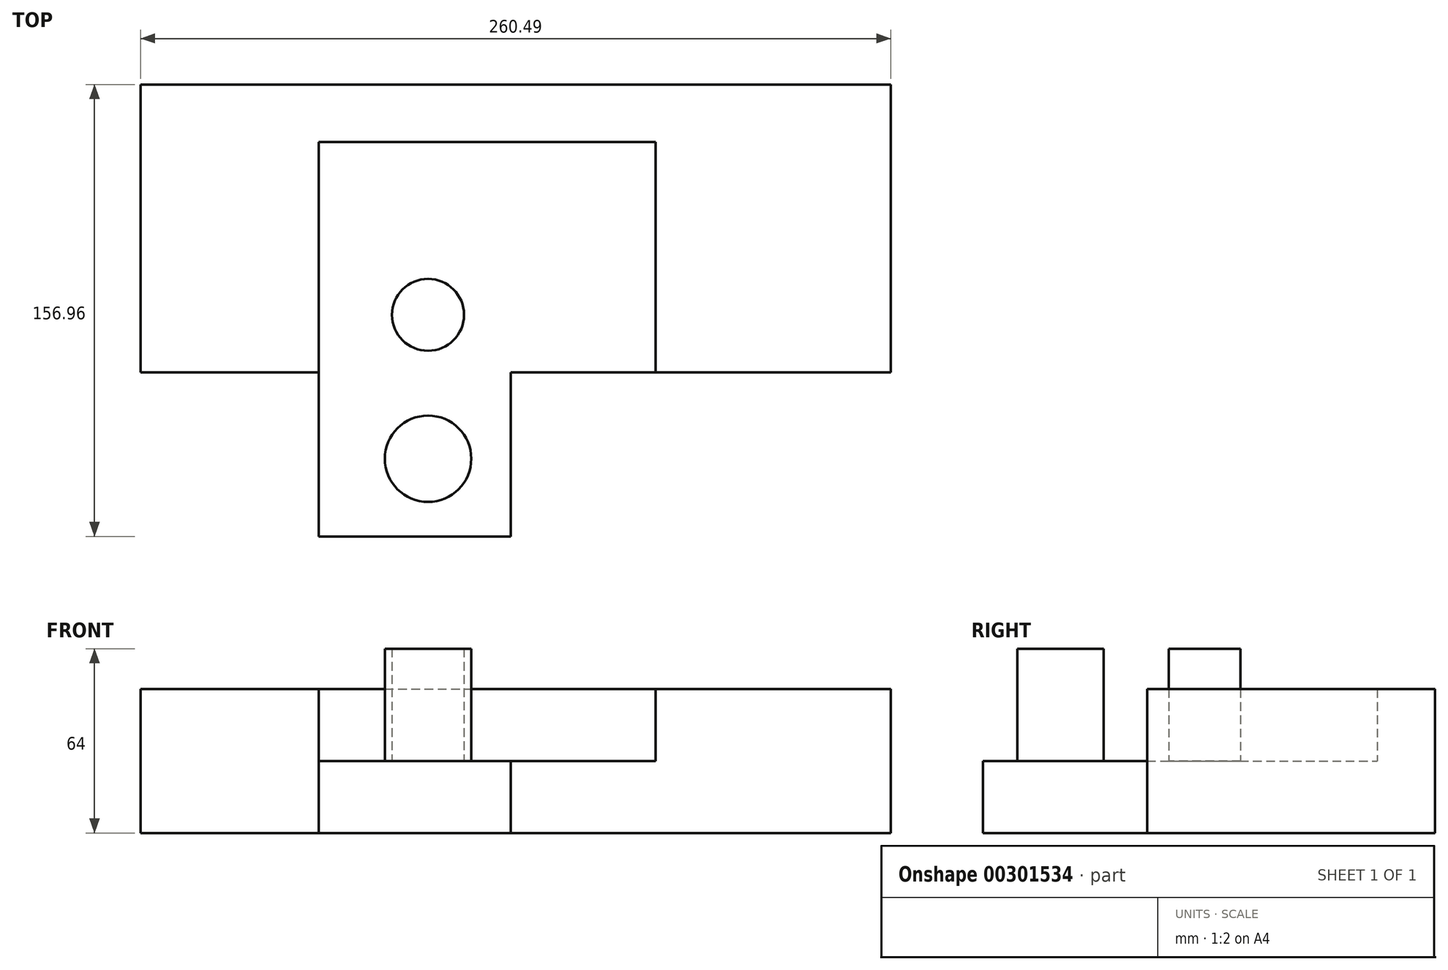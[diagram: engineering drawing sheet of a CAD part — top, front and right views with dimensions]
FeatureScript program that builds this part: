
annotation { "Feature Type Name" : "Feature", "Feature Type Description" : "" }
export const myFeature = defineFeature(function(context is Context, id is Id, definition is map)
    precondition{}
    {
        {
            var Q0;
            Q0=qCreatedBy(makeId("Top.planeOp"),FACE);
            var sketch = newSketch(context, id + "F0", { "sketchPlane" : qUnion([Q0])});
            skLineSegment(sketch, "E0", {"start": v(-120.1, 0) * mm, "end": v(-58.28, 0) * mm});
            skLineSegment(sketch, "E1", {"start": v(-58.28, 0) * mm, "end": v(-58.28, 80) * mm});
            skLineSegment(sketch, "E2", {"start": v(-58.28, 80) * mm, "end": v(58.72, 80) * mm});
            skLineSegment(sketch, "E3", {"start": v(58.72, 80) * mm, "end": v(58.72, 0) * mm});
            skLineSegment(sketch, "E4", {"start": v(58.72, 0) * mm, "end": v(140.4, 0) * mm});
            skLineSegment(sketch, "E5", {"start": v(140.4, 0) * mm, "end": v(140.4, 100) * mm});
            skLineSegment(sketch, "E6", {"start": v(140.4, 100) * mm, "end": v(-120.1, 100) * mm});
            skLineSegment(sketch, "E7", {"start": v(-120.1, 100) * mm, "end": v(-120.1, 0) * mm});
            skSolve(sketch);
        }
        {
            var Q0;
            Q0 = qSketchRegion(id + "F0", true);
            extrude(context, id + "F1", {"entities" : qUnion([Q0]), "depth" : 25 * mm});
        }
        {
            var Q0;
            Q0=makeQuery(id+"F1.opExtrude","CAP_FACE",FACE,{"disambiguationData":[OSD([sQuery(id+"F0.wireOp",EDGE,"E0"),sQuery(id+"F0.wireOp",EDGE,"E1"),sQuery(id+"F0.wireOp",EDGE,"E2"),sQuery(id+"F0.wireOp",EDGE,"E3"),sQuery(id+"F0.wireOp",EDGE,"E4"),sQuery(id+"F0.wireOp",EDGE,"E5"),sQuery(id+"F0.wireOp",EDGE,"E6"),sQuery(id+"F0.wireOp",EDGE,"E7")])],"isStart":true});
            var sketch = newSketch(context, id + "F2", { "sketchPlane" : qUnion([Q0])});
            skLineSegment(sketch, "E8.bottom", {"start": v(-120.1, 0) * mm, "end": v(-58.28, 0) * mm});
            skLineSegment(sketch, "E8.top", {"start": v(-120.1, -100) * mm, "end": v(140.4, -100) * mm});
            skLineSegment(sketch, "E8.left", {"start": v(-120.1, 0) * mm, "end": v(-120.1, -100) * mm});
            skLineSegment(sketch, "E8.right", {"start": v(140.4, 0) * mm, "end": v(140.4, -100) * mm});
            skLineSegment(sketch, "E9", {"start": v(-58.28, 0) * mm, "end": v(-58.28, 56.96) * mm});
            skLineSegment(sketch, "E10", {"start": v(-58.28, 56.96) * mm, "end": v(8.47, 56.96) * mm});
            skLineSegment(sketch, "E11", {"start": v(8.47, 56.96) * mm, "end": v(8.47, 0) * mm});
            skLineSegment(sketch, "E12.trimOffspring", {"start": v(8.47, 0) * mm, "end": v(140.4, 0) * mm});
            skSolve(sketch);
        }
        {
            var Q0;
            Q0 = qSketchRegion(id + "F2", true);
            extrude(context, id + "F3", {"entities" : qUnion([Q0]), "operationType" : NewBodyOperationType.ADD, "depth" : 25 * mm});
        }
        {
            var Q0;
            Q0=makeQuery(id+"F3.opExtrude","CAP_FACE",FACE,{"disambiguationData":[OSD([sQuery(id+"F2.wireOp",EDGE,"E8.bottom"),sQuery(id+"F2.wireOp",EDGE,"E8.top"),sQuery(id+"F2.wireOp",EDGE,"E8.left"),sQuery(id+"F2.wireOp",EDGE,"E8.right")])],"isStart":true});
            var sketch = newSketch(context, id + "F4", { "sketchPlane" : qUnion([Q0])});
            skCircle(sketch, "E13", {"center": v(-20.28, 20) * mm, "radius": 12.5 * mm});
            skCircle(sketch, "E14.0.4.0", {"center": v(-20.28, -30) * mm, "radius": 15 * mm});
            skLineSegment(sketch, "E15", {"start": v(-20.28, 20) * mm, "end": v(-20.28, -30) * mm});
            skSolve(sketch);
        }
        {
            var Q0;
            Q0 = qSketchRegion(id + "F4", true);
            extrude(context, id + "F5", {"entities" : qUnion([Q0]), "operationType" : NewBodyOperationType.ADD, "depth" : 39 * mm});
        }
    });
